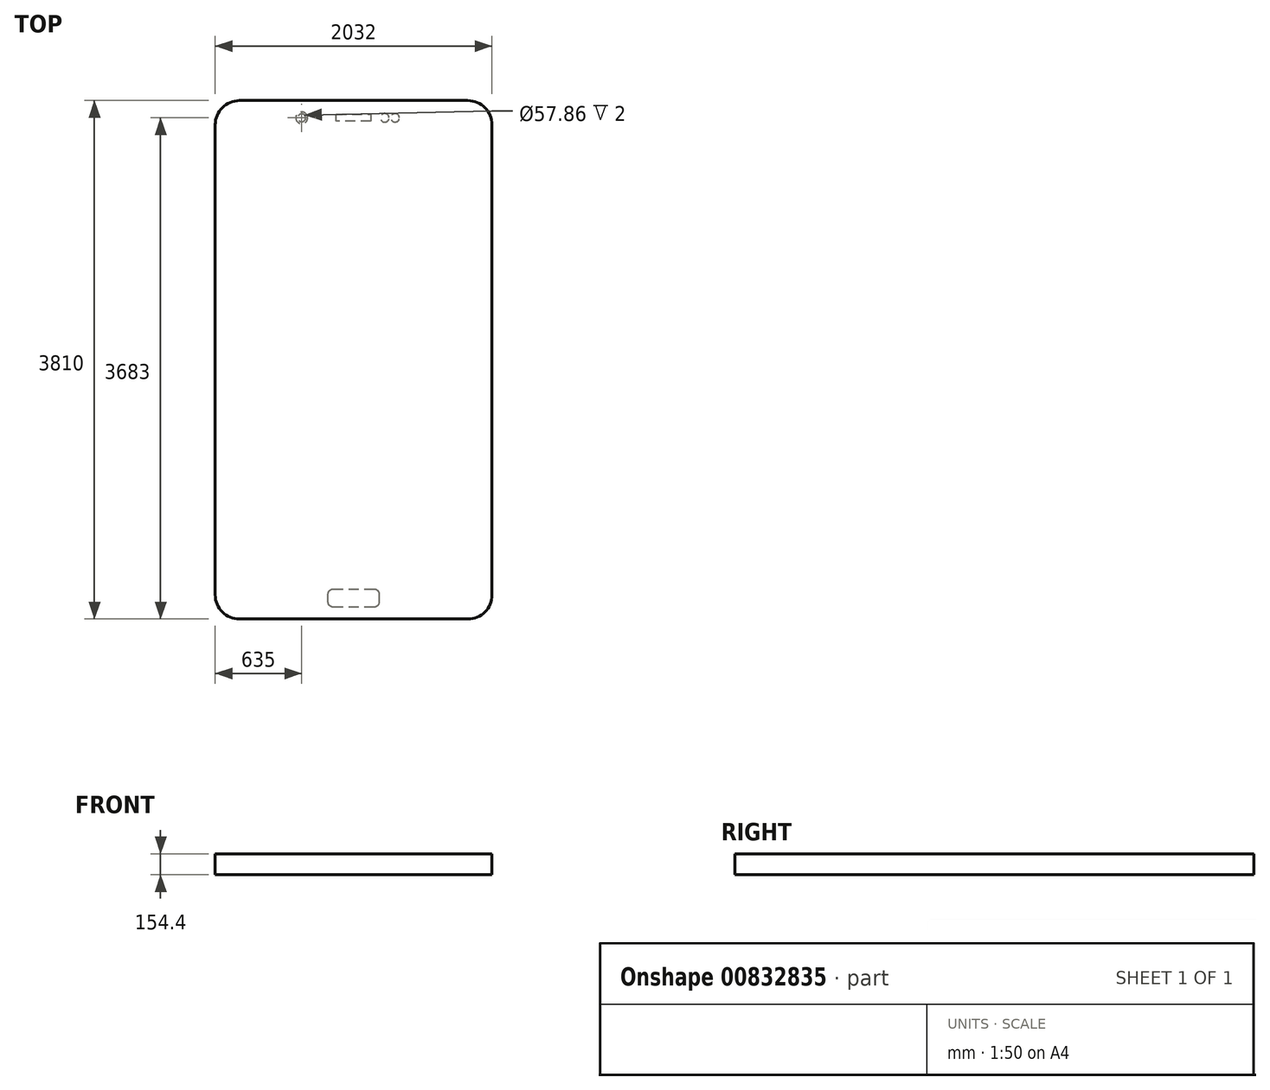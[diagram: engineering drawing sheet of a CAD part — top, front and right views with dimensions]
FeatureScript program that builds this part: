
annotation { "Feature Type Name" : "Feature", "Feature Type Description" : "" }
export const myFeature = defineFeature(function(context is Context, id is Id, definition is map)
    precondition{}
    {
        {
            var Q0;
            Q0=qCreatedBy(makeId("Top.planeOp"),FACE);
            var sketch = newSketch(context, id + "F0", { "sketchPlane" : qUnion([Q0])});
            skLineSegment(sketch, "E0.bottom", {"start": v(-177.8, 0) * mm, "end": v(-1854.2, 0) * mm});
            skLineSegment(sketch, "E0.top", {"start": v(-177.8, -3810) * mm, "end": v(-1854.2, -3810) * mm});
            skLineSegment(sketch, "E0.left", {"start": v(0, -177.8) * mm, "end": v(0, -3632.2) * mm});
            skLineSegment(sketch, "E0.right", {"start": v(-2032, -177.8) * mm, "end": v(-2032, -3632.2) * mm});
            skPoint(sketch, "E1.visualSharp", {"position": v(-2032, -3810) * mm});
            skArc(sketch, "E1.filletArc", {"start": v(-2032, -3632.2) * mm, "mid": v(-1979.92, -3757.92) * mm, "end": v(-1854.2, -3810) * mm});
            skPoint(sketch, "E2.visualSharp", {"position": v(0, -3810) * mm});
            skArc(sketch, "E2.filletArc", {"start": v(-177.8, -3810) * mm, "mid": v(-52.08, -3757.92) * mm, "end": v(0, -3632.2) * mm});
            skPoint(sketch, "E3.visualSharp", {"position": v(0, 0) * mm});
            skArc(sketch, "E3.filletArc", {"start": v(0, -177.8) * mm, "mid": v(-52.08, -52.08) * mm, "end": v(-177.8, 0) * mm});
            skPoint(sketch, "E4.visualSharp", {"position": v(-2032, 0) * mm});
            skArc(sketch, "E4.filletArc", {"start": v(-1854.2, 0) * mm, "mid": v(-1979.92, -52.08) * mm, "end": v(-2032, -177.8) * mm});
            skLineSegment(sketch, "E5", {"start": v(-1104.9, -466.16) * mm, "end": v(-927.1, -466.16) * mm});
            skLineSegment(sketch, "E6", {"start": v(-825.5, -567.76) * mm, "end": v(-825.5, -745.56) * mm});
            skLineSegment(sketch, "E7", {"start": v(-927.1, -847.16) * mm, "end": v(-1104.9, -847.16) * mm});
            skLineSegment(sketch, "E8", {"start": v(-1206.5, -745.56) * mm, "end": v(-1206.5, -567.76) * mm});
            skPoint(sketch, "E9.start.orphan", {"position": v(-2032, -381) * mm});
            skPoint(sketch, "E10.end.orphan", {"position": v(-1016, -381) * mm});
            skPoint(sketch, "E10.start.orphan", {"position": v(-1016, 0) * mm});
            skLineSegment(sketch, "E11", {"start": v(-647.7, -516.96) * mm, "end": v(-647.7, -796.36) * mm});
            skLineSegment(sketch, "E12", {"start": v(-596.9, -847.16) * mm, "end": v(-571.5, -847.16) * mm});
            skLineSegment(sketch, "E13", {"start": v(-520.7, -796.36) * mm, "end": v(-520.7, -516.96) * mm});
            skLineSegment(sketch, "E14", {"start": v(-571.5, -466.16) * mm, "end": v(-596.9, -466.16) * mm});
            skPoint(sketch, "E15.visualSharp", {"position": v(-1206.5, -466.16) * mm});
            skArc(sketch, "E15.filletArc", {"start": v(-1104.9, -466.16) * mm, "mid": v(-1176.74, -495.92) * mm, "end": v(-1206.5, -567.76) * mm});
            skPoint(sketch, "E16.visualSharp", {"position": v(-825.5, -466.16) * mm});
            skArc(sketch, "E16.filletArc", {"start": v(-825.5, -567.76) * mm, "mid": v(-855.26, -495.92) * mm, "end": v(-927.1, -466.16) * mm});
            skPoint(sketch, "E17.visualSharp", {"position": v(-825.5, -847.16) * mm});
            skArc(sketch, "E17.filletArc", {"start": v(-927.1, -847.16) * mm, "mid": v(-855.26, -817.4) * mm, "end": v(-825.5, -745.56) * mm});
            skPoint(sketch, "E18.visualSharp", {"position": v(-1206.5, -847.16) * mm});
            skArc(sketch, "E18.filletArc", {"start": v(-1206.5, -745.56) * mm, "mid": v(-1176.74, -817.4) * mm, "end": v(-1104.9, -847.16) * mm});
            skPoint(sketch, "E19.visualSharp", {"position": v(-647.7, -847.16) * mm});
            skArc(sketch, "E19.filletArc", {"start": v(-647.7, -796.36) * mm, "mid": v(-632.82, -832.28) * mm, "end": v(-596.9, -847.16) * mm});
            skPoint(sketch, "E20.visualSharp", {"position": v(-520.7, -847.16) * mm});
            skPoint(sketch, "E21.visualSharp", {"position": v(-520.7, -466.16) * mm});
            skArc(sketch, "E21.filletArc", {"start": v(-525.5, -468.99) * mm, "mid": v(-529.27, -466.88) * mm, "end": v(-533.53, -466.16) * mm});
            skPoint(sketch, "E22.visualSharp", {"position": v(-647.7, -466.16) * mm});
            skArc(sketch, "E22.filletArc", {"start": v(-634.87, -466.16) * mm, "mid": v(-639.13, -466.88) * mm, "end": v(-642.9, -468.99) * mm});
            skArc(sketch, "E23.filletArc", {"start": v(-596.9, -466.16) * mm, "mid": v(-632.82, -481.04) * mm, "end": v(-647.7, -516.96) * mm});
            skArc(sketch, "E24.filletArc", {"start": v(-520.7, -516.96) * mm, "mid": v(-535.58, -481.04) * mm, "end": v(-571.5, -466.16) * mm});
            skArc(sketch, "E25.0", {"start": v(-1104.9, -491.56) * mm, "mid": v(-1158.78, -513.88) * mm, "end": v(-1181.1, -567.76) * mm});
            skLineSegment(sketch, "E25.1", {"start": v(-1181.1, -745.56) * mm, "end": v(-1181.1, -567.76) * mm});
            skLineSegment(sketch, "E25.2", {"start": v(-1104.9, -491.56) * mm, "end": v(-927.1, -491.56) * mm});
            skArc(sketch, "E25.3", {"start": v(-1181.1, -745.56) * mm, "mid": v(-1158.78, -799.44) * mm, "end": v(-1104.9, -821.76) * mm});
            skArc(sketch, "E25.4", {"start": v(-850.9, -567.76) * mm, "mid": v(-873.22, -513.88) * mm, "end": v(-927.1, -491.56) * mm});
            skLineSegment(sketch, "E25.5", {"start": v(-850.9, -567.76) * mm, "end": v(-850.9, -745.56) * mm});
            skArc(sketch, "E25.6", {"start": v(-927.1, -821.76) * mm, "mid": v(-873.22, -799.44) * mm, "end": v(-850.9, -745.56) * mm});
            skLineSegment(sketch, "E25.7", {"start": v(-927.1, -821.76) * mm, "end": v(-1104.9, -821.76) * mm});
            skArc(sketch, "E26.filletArc", {"start": v(-571.5, -847.16) * mm, "mid": v(-535.58, -832.28) * mm, "end": v(-520.7, -796.36) * mm});
            skArc(sketch, "E27.0", {"start": v(-596.9, -478.86) * mm, "mid": v(-623.84, -490.02) * mm, "end": v(-635, -516.96) * mm});
            skLineSegment(sketch, "E27.1", {"start": v(-571.5, -478.86) * mm, "end": v(-596.9, -478.86) * mm});
            skLineSegment(sketch, "E27.2", {"start": v(-635, -516.96) * mm, "end": v(-635, -796.36) * mm});
            skArc(sketch, "E27.3", {"start": v(-533.4, -516.96) * mm, "mid": v(-544.56, -490.02) * mm, "end": v(-571.5, -478.86) * mm});
            skArc(sketch, "E27.4", {"start": v(-635, -796.36) * mm, "mid": v(-623.84, -823.3) * mm, "end": v(-596.9, -834.46) * mm});
            skLineSegment(sketch, "E27.5", {"start": v(-596.9, -834.46) * mm, "end": v(-571.5, -834.46) * mm});
            skArc(sketch, "E27.6", {"start": v(-571.5, -834.46) * mm, "mid": v(-544.56, -823.3) * mm, "end": v(-533.4, -796.36) * mm});
            skLineSegment(sketch, "E27.7", {"start": v(-533.4, -796.36) * mm, "end": v(-533.4, -516.96) * mm});
            skArc(sketch, "E28.0", {"start": v(-548.17, -516.96) * mm, "mid": v(-555, -500.46) * mm, "end": v(-571.5, -493.62) * mm});
            skLineSegment(sketch, "E28.1", {"start": v(-548.17, -546.5) * mm, "end": v(-548.17, -516.96) * mm});
            skLineSegment(sketch, "E28.2", {"start": v(-571.5, -493.62) * mm, "end": v(-596.9, -493.62) * mm});
            skArc(sketch, "E28.4", {"start": v(-596.9, -493.62) * mm, "mid": v(-613.4, -500.46) * mm, "end": v(-620.23, -516.96) * mm});
            skLineSegment(sketch, "E28.5", {"start": v(-620.23, -516.96) * mm, "end": v(-620.23, -546.5) * mm});
            skLineSegment(sketch, "E29", {"start": v(-584.2, -569.82) * mm, "end": v(-596.9, -569.82) * mm});
            skLineSegment(sketch, "E30", {"start": v(-584.2, -569.82) * mm, "end": v(-571.5, -569.82) * mm});
            skPoint(sketch, "E31.start.orphan", {"position": v(-584.2, -493.62) * mm});
            skArc(sketch, "E32.filletArc", {"start": v(-620.23, -565.72) * mm, "mid": v(-619.03, -568.62) * mm, "end": v(-616.13, -569.82) * mm});
            skArc(sketch, "E33.filletArc", {"start": v(-620.23, -546.5) * mm, "mid": v(-613.4, -562.99) * mm, "end": v(-596.9, -569.82) * mm});
            skArc(sketch, "E34.filletArc", {"start": v(-571.5, -569.82) * mm, "mid": v(-555, -562.99) * mm, "end": v(-548.17, -546.5) * mm});
            skArc(sketch, "E35.0", {"start": v(-621.8, -796.36) * mm, "mid": v(-614.5, -813.96) * mm, "end": v(-596.9, -821.25) * mm});
            skLineSegment(sketch, "E35.1", {"start": v(-621.8, -629.91) * mm, "end": v(-621.8, -796.36) * mm});
            skLineSegment(sketch, "E35.2", {"start": v(-596.9, -821.25) * mm, "end": v(-571.5, -821.25) * mm});
            skArc(sketch, "E35.4", {"start": v(-571.5, -821.25) * mm, "mid": v(-553.9, -813.96) * mm, "end": v(-546.6, -796.36) * mm});
            skLineSegment(sketch, "E35.5", {"start": v(-546.6, -796.36) * mm, "end": v(-546.6, -629.91) * mm});
            skLineSegment(sketch, "E36", {"start": v(-598.46, -606.58) * mm, "end": v(-569.94, -606.58) * mm});
            skArc(sketch, "E37.filletArc", {"start": v(-598.46, -606.58) * mm, "mid": v(-614.96, -613.41) * mm, "end": v(-621.8, -629.91) * mm});
            skArc(sketch, "E38.filletArc", {"start": v(-546.6, -629.91) * mm, "mid": v(-553.44, -613.41) * mm, "end": v(-569.94, -606.58) * mm});
            skText(sketch, "E39", { "text": "SAMSUNG", "fontName": "OpenSans-Bold.ttf"});
            skPoint(sketch, "E40.end.orphan", {"position": v(-1016, -1355.16) * mm});
            skPoint(sketch, "E40.start.orphan", {"position": v(-1016, -847.16) * mm});
            const initialGuessF0  = {"E39": [-1.524, -1.5011, 1, 0, 0.14595]};
            skSetInitialGuess(sketch, initialGuessF0);
            skSolve(sketch);
        }
        {
            var Q0;
            Q0=makeQuery(id+"F0.imprint","IMPRINT",FACE,{"disambiguationData":[TD([[makeQuery(id+"F0.imprint","IMPRINT",EDGE,{"derivedFrom":sQuery(id+"F0.wireOp",EDGE,"E0.bottom")}),1.0]])]});
            var Q1;
            Q1=makeQuery(id+"F0.imprint","IMPRINT",FACE,{"disambiguationData":[TD([[makeQuery(id+"F0.imprint","IMPRINT",EDGE,{"derivedFrom":sQuery(id+"F0.wireOp",EDGE,"E27.0")}),1.0]])]});
            var Q2;
            Q2=makeQuery(id+"F0.imprint","IMPRINT",FACE,{"disambiguationData":[TD([[makeQuery(id+"F0.imprint","IMPRINT",EDGE,{"derivedFrom":sQuery(id+"F0.wireOp",EDGE,"E35.0")}),1.0]])]});
            var Q3;
            Q3=makeQuery(id+"F0.imprint","IMPRINT",FACE,{"disambiguationData":[TD([[makeQuery(id+"F0.imprint","IMPRINT",EDGE,{"derivedFrom":sQuery(id+"F0.wireOp",EDGE,"E25.0")}),1.0]])]});
            var Q4;
            Q4=makeQuery(id+"F0.imprint","IMPRINT",FACE,{"disambiguationData":[TD([[makeQuery(id+"F0.imprint","IMPRINT",EDGE,{"derivedFrom":sQuery(id+"F0.wireOp",EDGE,"E5")}),-1.0]])]});
            var Q5;
            Q5=makeQuery(id+"F0.imprint","IMPRINT",FACE,{"disambiguationData":[TD([[makeQuery(id+"F0.imprint","IMPRINT",EDGE,{"derivedFrom":sQuery(id+"F0.wireOp",EDGE,"E11")}),1.0]])]});
            var Q6;
            Q6=makeQuery(id+"F0.imprint","IMPRINT",FACE,{"disambiguationData":[TD([[makeQuery(id+"F0.imprint","IMPRINT",EDGE,{"derivedFrom":sQuery(id+"F0.wireOp",EDGE,"E28.0")}),1.0]])]});
            var Q7;
            Q7=makeQuery(id+"F0.imprint","IMPRINT",FACE,{"disambiguationData":[TD([[makeQuery(id+"F0.imprint","IMPRINT",EDGE,{"derivedFrom":sQuery(id+"F0.wireOp",EDGE,"E39.sketch_text.stroke-40")}),-1.0]])]});
            var Q8;
            Q8=makeQuery(id+"F0.imprint","IMPRINT",FACE,{"disambiguationData":[TD([[makeQuery(id+"F0.imprint","IMPRINT",EDGE,{"derivedFrom":sQuery(id+"F0.wireOp",EDGE,"E39.sketch_text.stroke-28")}),-1.0]])]});
            var Q9;
            Q9=makeQuery(id+"F0.imprint","IMPRINT",FACE,{"disambiguationData":[TD([[makeQuery(id+"F0.imprint","IMPRINT",EDGE,{"derivedFrom":sQuery(id+"F0.wireOp",EDGE,"E39.sketch_text.stroke-116")}),-1.0]])]});
            var Q10;
            Q10=makeQuery(id+"F0.imprint","IMPRINT",FACE,{"disambiguationData":[TD([[makeQuery(id+"F0.imprint","IMPRINT",EDGE,{"derivedFrom":sQuery(id+"F0.wireOp",EDGE,"E39.sketch_text.stroke-87")}),-1.0]])]});
            var Q11;
            Q11=makeQuery(id+"F0.imprint","IMPRINT",FACE,{"disambiguationData":[TD([[makeQuery(id+"F0.imprint","IMPRINT",EDGE,{"derivedFrom":sQuery(id+"F0.wireOp",EDGE,"E39.sketch_text.stroke-59")}),-1.0]])]});
            var Q12;
            Q12=makeQuery(id+"F0.imprint","IMPRINT",FACE,{"disambiguationData":[TD([[makeQuery(id+"F0.imprint","IMPRINT",EDGE,{"derivedFrom":sQuery(id+"F0.wireOp",EDGE,"E39.sketch_text.stroke-102")}),-1.0]])]});
            var Q13;
            Q13=makeQuery(id+"F0.imprint","IMPRINT",FACE,{"disambiguationData":[TD([[makeQuery(id+"F0.imprint","IMPRINT",EDGE,{"derivedFrom":sQuery(id+"F0.wireOp",EDGE,"E39.sketch_text.stroke-0")}),-1.0]])]});
            var Q14;
            Q14=makeQuery(id+"F0.imprint","IMPRINT",FACE,{"disambiguationData":[TD([[makeQuery(id+"F0.imprint","IMPRINT",EDGE,{"derivedFrom":sQuery(id+"F0.wireOp",EDGE,"E39.sketch_text.stroke-36")}),1.0]])]});
            var Q15;
            Q15 = qSketchRegion(id + "F2", true);
            extrude(context, id + "F1", {"entities" : qUnion([Q0, Q1, Q2, Q3, Q4, Q5, Q6, Q7, Q8, Q9, Q10, Q11, Q12, Q13, Q14, Q15]), "oppositeDirection" : true, "depth" : 152.4 * mm, "offsetDistance" : 25.4 * mm});
        }
        {
            var Q0;
            Q0=makeQuery(id+"F0.imprint","IMPRINT",FACE,{"disambiguationData":[TD([[makeQuery(id+"F0.imprint","IMPRINT",EDGE,{"derivedFrom":sQuery(id+"F0.wireOp",EDGE,"E0.bottom")}),1.0]])]});
            var sketch = newSketch(context, id + "F2", { "sketchPlane" : qUnion([Q0])});
            skLineSegment(sketch, "E41", {"start": v(-1016, -3719.45) * mm, "end": v(-863.6, -3719.45) * mm});
            skLineSegment(sketch, "E42", {"start": v(-825.5, -3681.35) * mm, "end": v(-825.5, -3630.55) * mm});
            skLineSegment(sketch, "E43", {"start": v(-863.6, -3592.45) * mm, "end": v(-1168.4, -3592.45) * mm});
            skLineSegment(sketch, "E44", {"start": v(-1206.5, -3630.55) * mm, "end": v(-1206.5, -3681.35) * mm});
            skLineSegment(sketch, "E45", {"start": v(-1168.4, -3719.45) * mm, "end": v(-1016, -3719.45) * mm});
            skPoint(sketch, "E46.visualSharp", {"position": v(-1206.5, -3592.45) * mm});
            skArc(sketch, "E46.filletArc", {"start": v(-1168.4, -3592.45) * mm, "mid": v(-1195.34, -3603.61) * mm, "end": v(-1206.5, -3630.55) * mm});
            skPoint(sketch, "E47.visualSharp", {"position": v(-1206.5, -3719.45) * mm});
            skArc(sketch, "E47.filletArc", {"start": v(-1206.5, -3681.35) * mm, "mid": v(-1195.34, -3708.3) * mm, "end": v(-1168.4, -3719.45) * mm});
            skPoint(sketch, "E48.visualSharp", {"position": v(-825.5, -3719.45) * mm});
            skArc(sketch, "E48.filletArc", {"start": v(-863.6, -3719.45) * mm, "mid": v(-836.66, -3708.3) * mm, "end": v(-825.5, -3681.35) * mm});
            skPoint(sketch, "E49.visualSharp", {"position": v(-825.5, -3592.45) * mm});
            skArc(sketch, "E49.filletArc", {"start": v(-825.5, -3630.55) * mm, "mid": v(-836.66, -3603.61) * mm, "end": v(-863.6, -3592.45) * mm});
            skLineSegment(sketch, "E50", {"start": v(-1016, -3592.45) * mm, "end": v(-1016, -3516.25) * mm});
            skLineSegment(sketch, "E51", {"start": v(-1016, 0) * mm, "end": v(-1016, -101.6) * mm});
            skLineSegment(sketch, "E52", {"start": v(-1016, -101.6) * mm, "end": v(-889, -101.6) * mm});
            skLineSegment(sketch, "E53", {"start": v(-889, -101.6) * mm, "end": v(-889, -152.4) * mm});
            skLineSegment(sketch, "E54", {"start": v(-889, -152.4) * mm, "end": v(-1143, -152.4) * mm});
            skLineSegment(sketch, "E55", {"start": v(-1143, -152.4) * mm, "end": v(-1143, -101.6) * mm});
            skLineSegment(sketch, "E56", {"start": v(-1143, -101.6) * mm, "end": v(-1016, -101.6) * mm});
            skCircle(sketch, "E57", {"center": v(-711.2, -127) * mm, "radius": 31.35 * mm});
            skCircle(sketch, "E58", {"center": v(-787.4, -127) * mm, "radius": 31.61 * mm});
            skPoint(sketch, "E59.orphan", {"position": v(-889, -127) * mm});
            skCircle(sketch, "E60", {"center": v(-1397, -127) * mm, "radius": 43.52 * mm});
            skCircle(sketch, "E61.0", {"center": v(-1397, -127) * mm, "radius": 28.93 * mm});
            skPoint(sketch, "E62.orphan", {"position": v(-1143, -127) * mm});
            skLineSegment(sketch, "E63", {"start": v(-1016, -152.4) * mm, "end": v(-1016, -304.8) * mm});
            skLineSegment(sketch, "E64", {"start": v(-1016, -304.8) * mm, "end": v(-25.4, -304.8) * mm});
            skLineSegment(sketch, "E65", {"start": v(-25.4, -304.8) * mm, "end": v(-25.4, -3516.25) * mm});
            skLineSegment(sketch, "E66", {"start": v(-25.4, -3516.25) * mm, "end": v(-2006.6, -3516.25) * mm});
            skLineSegment(sketch, "E67", {"start": v(-2006.6, -3516.25) * mm, "end": v(-2006.6, -304.8) * mm});
            skLineSegment(sketch, "E68", {"start": v(-2006.6, -304.8) * mm, "end": v(-1016, -304.8) * mm});
            skSolve(sketch);
        }
        {
            var Q0;
            Q0=makeQuery(id+"F2.imprint","IMPRINT",FACE,{"disambiguationData":[TD([[makeQuery(id+"F2.imprint","IMPRINT",EDGE,{"derivedFrom":sQuery(id+"F2.wireOp",EDGE,"E57")}),1.0]])]});
            var Q1;
            Q1=makeQuery(id+"F2.imprint","IMPRINT",FACE,{"disambiguationData":[TD([[makeQuery(id+"F2.imprint","IMPRINT",EDGE,{"derivedFrom":sQuery(id+"F2.wireOp",EDGE,"E58")}),1.0]])]});
            var Q2;
            Q2=makeQuery(id+"F2.imprint","IMPRINT",FACE,{"disambiguationData":[TD([[makeQuery(id+"F2.imprint","IMPRINT",EDGE,{"derivedFrom":sQuery(id+"F2.wireOp",EDGE,"E41")}),-1.0]])]});
            var Q3;
            Q3=makeQuery(id+"F2.imprint","IMPRINT",FACE,{"disambiguationData":[TD([[makeQuery(id+"F2.imprint","IMPRINT",EDGE,{"derivedFrom":sQuery(id+"F2.wireOp",EDGE,"E64")}),-1.0]])]});
            var Q4;
            Q4=makeQuery(id+"F2.imprint","IMPRINT",FACE,{"disambiguationData":[TD([[makeQuery(id+"F2.imprint","IMPRINT",EDGE,{"derivedFrom":makeQuery(id+"F0.imprint","IMPRINT",EDGE,{"derivedFrom":sQuery(id+"F0.wireOp",EDGE,"E11")})}),1.0]])]});
            var Q5;
            Q5=makeQuery(id+"F2.imprint","IMPRINT",FACE,{"disambiguationData":[TD([[makeQuery(id+"F2.imprint","IMPRINT",EDGE,{"derivedFrom":sQuery(id+"F2.wireOp",EDGE,"E52")}),-1.0]])]});
            var Q6;
            Q6=makeQuery(id+"F2.imprint","IMPRINT",FACE,{"disambiguationData":[TD([[makeQuery(id+"F2.imprint","IMPRINT",EDGE,{"derivedFrom":makeQuery(id+"F0.imprint","IMPRINT",EDGE,{"derivedFrom":sQuery(id+"F0.wireOp",EDGE,"E39.sketch_text.stroke-102")})}),-1.0]])]});
            var Q7;
            Q7=makeQuery(id+"F2.imprint","IMPRINT",FACE,{"disambiguationData":[TD([[makeQuery(id+"F2.imprint","IMPRINT",EDGE,{"derivedFrom":makeQuery(id+"F0.imprint","IMPRINT",EDGE,{"derivedFrom":sQuery(id+"F0.wireOp",EDGE,"E39.sketch_text.stroke-87")})}),-1.0]])]});
            var Q8;
            Q8=makeQuery(id+"F2.imprint","IMPRINT",FACE,{"disambiguationData":[TD([[makeQuery(id+"F2.imprint","IMPRINT",EDGE,{"derivedFrom":makeQuery(id+"F0.imprint","IMPRINT",EDGE,{"derivedFrom":sQuery(id+"F0.wireOp",EDGE,"E39.sketch_text.stroke-28")})}),-1.0]])]});
            var Q9;
            Q9=makeQuery(id+"F2.imprint","IMPRINT",FACE,{"disambiguationData":[TD([[makeQuery(id+"F2.imprint","IMPRINT",EDGE,{"derivedFrom":makeQuery(id+"F0.imprint","IMPRINT",EDGE,{"derivedFrom":sQuery(id+"F0.wireOp",EDGE,"E39.sketch_text.stroke-0")})}),-1.0]])]});
            var Q10;
            Q10=makeQuery(id+"F2.imprint","IMPRINT",FACE,{"disambiguationData":[TD([[makeQuery(id+"F2.imprint","IMPRINT",EDGE,{"derivedFrom":makeQuery(id+"F0.imprint","IMPRINT",EDGE,{"derivedFrom":sQuery(id+"F0.wireOp",EDGE,"E39.sketch_text.stroke-116")})}),-1.0]])]});
            var Q11;
            Q11=makeQuery(id+"F2.imprint","IMPRINT",FACE,{"disambiguationData":[TD([[makeQuery(id+"F2.imprint","IMPRINT",EDGE,{"derivedFrom":makeQuery(id+"F0.imprint","IMPRINT",EDGE,{"derivedFrom":sQuery(id+"F0.wireOp",EDGE,"E39.sketch_text.stroke-40")})}),-1.0]])]});
            var Q12;
            Q12=makeQuery(id+"F2.imprint","IMPRINT",FACE,{"disambiguationData":[TD([[makeQuery(id+"F2.imprint","IMPRINT",EDGE,{"derivedFrom":makeQuery(id+"F0.imprint","IMPRINT",EDGE,{"derivedFrom":sQuery(id+"F0.wireOp",EDGE,"E39.sketch_text.stroke-59")})}),-1.0]])]});
            var Q13;
            Q13=makeQuery(id+"F2.imprint","IMPRINT",FACE,{"disambiguationData":[TD([[makeQuery(id+"F2.imprint","IMPRINT",EDGE,{"derivedFrom":sQuery(id+"F2.wireOp",EDGE,"E41")}),1.0]])]});
            var Q14;
            Q14=makeQuery(id+"F2.imprint","IMPRINT",FACE,{"disambiguationData":[TD([[makeQuery(id+"F2.imprint","IMPRINT",EDGE,{"derivedFrom":makeQuery(id+"F0.imprint","IMPRINT",EDGE,{"derivedFrom":sQuery(id+"F0.wireOp",EDGE,"E5")})}),-1.0]])]});
            var Q15;
            Q15=makeQuery(id+"F2.imprint","IMPRINT",FACE,{"disambiguationData":[TD([[makeQuery(id+"F2.imprint","IMPRINT",EDGE,{"derivedFrom":sQuery(id+"F2.wireOp",EDGE,"E60")}),1.0]])]});
            var Q16;
            Q16=makeQuery(id+"F2.imprint","IMPRINT",FACE,{"disambiguationData":[TD([[makeQuery(id+"F2.imprint","IMPRINT",EDGE,{"derivedFrom":sQuery(id+"F2.wireOp",EDGE,"E61.0")}),1.0]])]});
            extrude(context, id + "F3", {"entities" : qUnion([Q0, Q1, Q2, Q3, Q4, Q5, Q6, Q7, Q8, Q9, Q10, Q11, Q12, Q13, Q14, Q15, Q16]), "oppositeDirection" : true, "depth" : 152.4 * mm, "offsetDistance" : 25.4 * mm});
        }
        {
            var Q0;
            Q0=makeQuery(id+"F3.opExtrude","SWEPT_BODY",BODY,{"disambiguationData":[OSD([sQuery(id+"F0.wireOp",EDGE,"E0.bottom"),sQuery(id+"F0.wireOp",EDGE,"E0.top"),sQuery(id+"F0.wireOp",EDGE,"E0.left"),sQuery(id+"F0.wireOp",EDGE,"E0.right"),sQuery(id+"F0.wireOp",EDGE,"E1.filletArc"),sQuery(id+"F0.wireOp",EDGE,"E2.filletArc"),sQuery(id+"F0.wireOp",EDGE,"E3.filletArc"),sQuery(id+"F0.wireOp",EDGE,"E4.filletArc")])]});
            deleteBodies(context, id + "F4", {"entities" : qUnion([Q0])});
        }
        {
            var Q0;
            Q0=makeQuery(id+"F2.imprint","IMPRINT",FACE,{"disambiguationData":[TD([[makeQuery(id+"F2.imprint","IMPRINT",EDGE,{"derivedFrom":sQuery(id+"F2.wireOp",EDGE,"E52")}),-1.0]])]});
            var Q1;
            Q1=makeQuery(id+"F2.imprint","IMPRINT",FACE,{"disambiguationData":[TD([[makeQuery(id+"F2.imprint","IMPRINT",EDGE,{"derivedFrom":sQuery(id+"F2.wireOp",EDGE,"E58")}),1.0]])]});
            var Q2;
            Q2=makeQuery(id+"F2.imprint","IMPRINT",FACE,{"disambiguationData":[TD([[makeQuery(id+"F2.imprint","IMPRINT",EDGE,{"derivedFrom":sQuery(id+"F2.wireOp",EDGE,"E57")}),1.0]])]});
            var Q3;
            Q3=makeQuery(id+"F2.imprint","IMPRINT",FACE,{"disambiguationData":[TD([[makeQuery(id+"F2.imprint","IMPRINT",EDGE,{"derivedFrom":sQuery(id+"F2.wireOp",EDGE,"E60")}),1.0]])]});
            var Q4;
            Q4=makeQuery(id+"F2.imprint","IMPRINT",FACE,{"disambiguationData":[TD([[makeQuery(id+"F2.imprint","IMPRINT",EDGE,{"derivedFrom":sQuery(id+"F2.wireOp",EDGE,"E41")}),1.0]])]});
            extrude(context, id + "F5", {"entities" : qUnion([Q0, Q1, Q2, Q3, Q4]), "operationType" : NewBodyOperationType.ADD, "oppositeDirection" : true, "depth" : 154.4 * mm, "offsetDistance" : 25 * mm});
        }
    });
